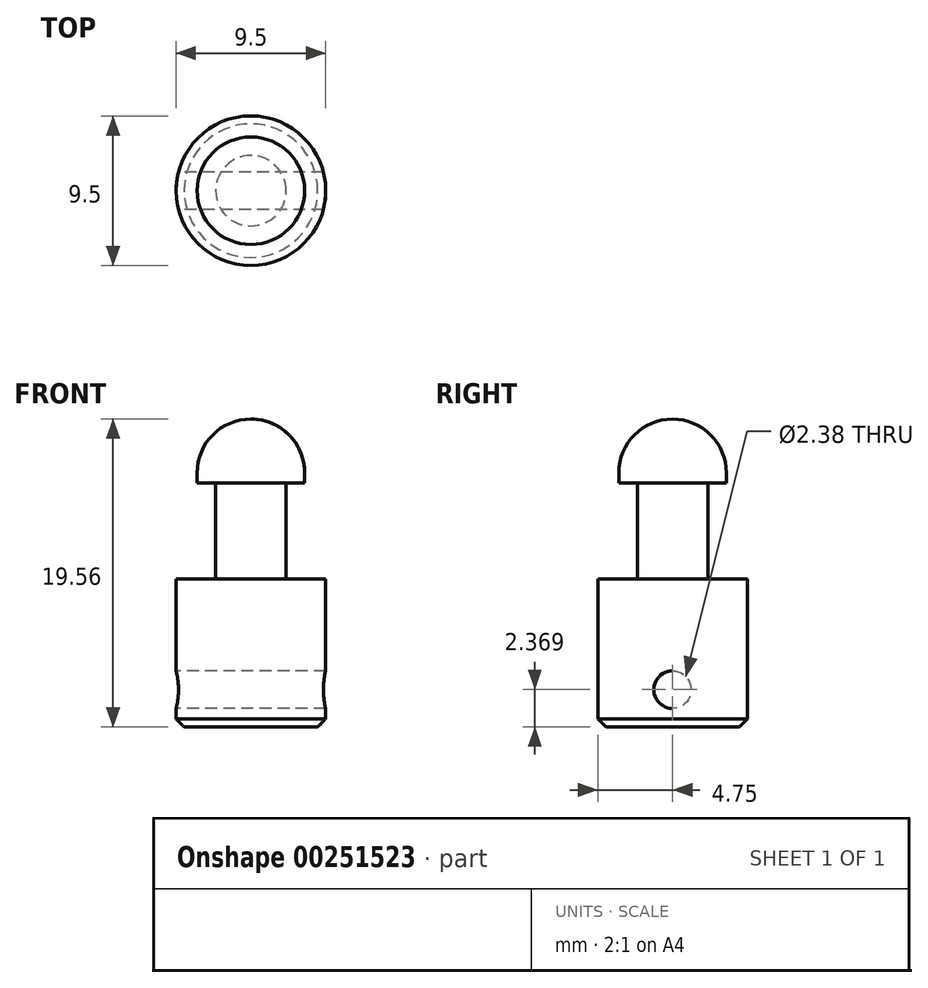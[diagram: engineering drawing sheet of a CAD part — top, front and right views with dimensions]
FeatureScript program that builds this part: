
annotation { "Feature Type Name" : "Feature", "Feature Type Description" : "" }
export const myFeature = defineFeature(function(context is Context, id is Id, definition is map)
    precondition{}
    {
        {
            var Q0;
            Q0=qCreatedBy(makeId("Top.planeOp"),FACE);
            var sketch = newSketch(context, id + "F0", { "sketchPlane" : qUnion([Q0])});
            skCircle(sketch, "E0", {"center": v(0, 0) * mm, "radius": 4.75 * mm});
            skSolve(sketch);
        }
        {
            var Q0;
            Q0=makeQuery(id+"F0.imprint","IMPRINT",FACE,{"disambiguationData":[TD([[makeQuery(id+"F0.imprint","IMPRINT",EDGE,{"derivedFrom":sQuery(id+"F0.wireOp",EDGE,"E0")}),1.0]])]});
            extrude(context, id + "F1", {"entities" : qUnion([Q0]), "flatOperationType" : FlatOperationType.REMOVE, "thickness1" : 6.35 * mm, "thickness2" : 0 * mm, "thickness" : 6.35 * mm, "offsetDistance" : 25.4 * mm, "startOffsetBound" : StartOffsetType.BLIND, "startOffsetDistance" : 25.4 * mm, "depth" : 9.4 * mm, "domain" : OperationDomain.MODEL});
        }
        {
            var Q0;
            Q0=makeQuery(id+"F1.opExtrude","CAP_FACE",FACE,{"disambiguationData":[OSD([sQuery(id+"F0.wireOp",EDGE,"E0")])],"isStart":false});
            var sketch = newSketch(context, id + "F2", { "sketchPlane" : qUnion([Q0])});
            skCircle(sketch, "E1", {"center": v(0, 0) * mm, "radius": 2.24 * mm});
            skSolve(sketch);
        }
        {
            var Q0;
            Q0=makeQuery(id+"F2.imprint","IMPRINT",FACE,{"disambiguationData":[TD([[makeQuery(id+"F2.imprint","IMPRINT",EDGE,{"derivedFrom":sQuery(id+"F2.wireOp",EDGE,"E1")}),1.0]])]});
            extrude(context, id + "F3", {"entities" : qUnion([Q0]), "operationType" : NewBodyOperationType.ADD, "depth" : 6.1 * mm});
        }
        {
            var Q0;
            Q0=makeQuery(id+"F3.opExtrude","CAP_FACE",FACE,{"disambiguationData":[OSD([sQuery(id+"F2.wireOp",EDGE,"E1")])],"isStart":false});
            var sketch = newSketch(context, id + "F4", { "sketchPlane" : qUnion([Q0])});
            skCircle(sketch, "E2", {"center": v(0, 0) * mm, "radius": 3.42 * mm});
            skSolve(sketch);
        }
        {
            var Q0;
            Q0=makeQuery(id+"F4.imprint","IMPRINT",FACE,{"disambiguationData":[TD([[makeQuery(id+"F4.imprint","IMPRINT",EDGE,{"derivedFrom":sQuery(id+"F4.wireOp",EDGE,"E2")}),1.0]])]});
            var Q1;
            Q1=makeQuery(id+"F4.imprint","IMPRINT",FACE,{"disambiguationData":[TD([[makeQuery(id+"F4.imprint","IMPRINT",EDGE,{"derivedFrom":makeQuery(id+"F3.opExtrude","CAP_EDGE",EDGE,{"disambiguationData":[OSD([sQuery(id+"F2.wireOp",EDGE,"E1")])],"isStart":false})}),1.0]])]});
            extrude(context, id + "F5", {"entities" : qUnion([Q0, Q1]), "operationType" : NewBodyOperationType.ADD, "depth" : 4.06 * mm});
        }
        {
            var Q0;
            Q0=makeQuery(id+"F5.opExtrude","CAP_EDGE",EDGE,{"disambiguationData":[OSD([sQuery(id+"F4.wireOp",EDGE,"E2")])],"isStart":false});
            fillet(context, id + "F6", {"entities" : qUnion([Q0]), "radius" : 3.42 * mm, "allowEdgeOverflow" : false});
        }
        {
            var Q0;
            Q0=qCreatedBy(makeId("Right.planeOp"),FACE);
            cPlane(context, id + "F7", {"entities" : qUnion([Q0]), "cplaneType" : CPlaneType.OFFSET, "offset" : 4.75 * mm, "width" : 152.4 * mm, "height" : 152.4 * mm});
        }
        {
            var Q0;
            Q0=qCreatedBy(id+"F7.planeOp",FACE);
            var sketch = newSketch(context, id + "F8", { "sketchPlane" : qUnion([Q0])});
            skPoint(sketch, "E3", {"position": v(0, 2.37) * mm});
            skSolve(sketch);
        }
        {
            var Q0;
            Q0=sQuery(id+"F8.wireOp",VERTEX,"E3");
            var Q1;
            Q1=makeQuery(id+"F1.opExtrude","SWEPT_BODY",BODY,{"disambiguationData":[OSD([sQuery(id+"F0.wireOp",EDGE,"E0")])]});
            hole(context, id + "F9", {"style" : HoleStyle.SIMPLE, "endStyle" : HoleEndStyle.THROUGH, "holeDiameter" : 2.38 * mm, "tappedDepth" : 12.7 * mm, "tapClearance" : 3, "locations" : qUnion([Q0]), "scope" : qUnion([Q1]), "startStyle" : HoleStartStyle.SKETCH});
        }
        {
            var Q0;
            Q0=makeQuery(id+"F1.opExtrude","CAP_EDGE",EDGE,{"disambiguationData":[OSD([sQuery(id+"F0.wireOp",EDGE,"E0")])],"isStart":true});
            chamfer(context, id + "F10", {"entities" : qUnion([Q0]), "width" : 0.5 * mm, "tangentPropagation" : true});
        }
    });
